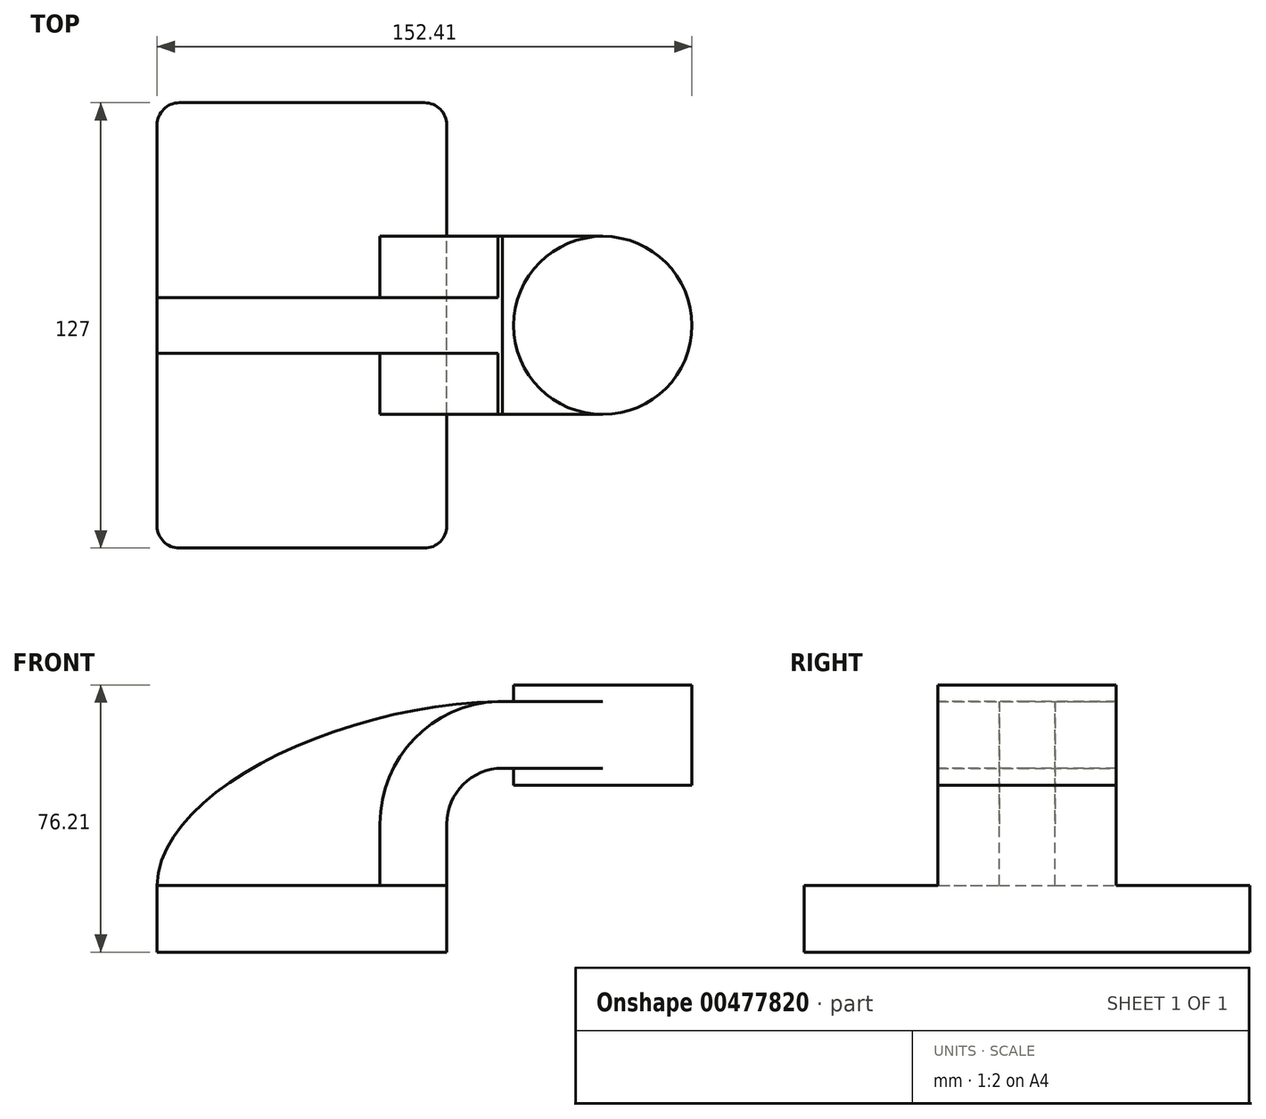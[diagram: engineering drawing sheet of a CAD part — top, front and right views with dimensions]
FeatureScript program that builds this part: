
annotation { "Feature Type Name" : "Feature", "Feature Type Description" : "" }
export const myFeature = defineFeature(function(context is Context, id is Id, definition is map)
    precondition{}
    {
        {
            var Q0;
            Q0=qCreatedBy(makeId("Front.planeOp"),FACE);
            var sketch = newSketch(context, id + "F0", { "sketchPlane" : qUnion([Q0])});
            skLineSegment(sketch, "E0.bottom", {"start": v(60.32, 66.67) * mm, "end": v(111.12, 66.67) * mm});
            skLineSegment(sketch, "E0.top", {"start": v(60.32, 38.1) * mm, "end": v(111.12, 38.1) * mm});
            skLineSegment(sketch, "E0.right", {"start": v(111.12, 66.68) * mm, "end": v(111.12, 38.1) * mm});
            skPoint(sketch, "E0.middle", {"position": v(85.72, 52.39) * mm});
            skLineSegment(sketch, "E1.bottom", {"start": v(-41.28, 9.52) * mm, "end": v(41.27, 9.53) * mm});
            skLineSegment(sketch, "E1.top", {"start": v(-41.28, -9.53) * mm, "end": v(41.28, -9.53) * mm});
            skLineSegment(sketch, "E1.left", {"start": v(-41.28, 9.52) * mm, "end": v(-41.28, -9.53) * mm});
            skLineSegment(sketch, "E1.right", {"start": v(41.28, 9.53) * mm, "end": v(41.28, -9.52) * mm});
            skPoint(sketch, "E1.middle", {"position": v(0, 0) * mm});
            skLineSegment(sketch, "E2", {"start": v(41.27, 9.53) * mm, "end": v(41.27, 27.06) * mm});
            skArc(sketch, "E3", {"start": v(41.28, 27.06) * mm, "mid": v(45.92, 38.29) * mm, "end": v(57.15, 42.93) * mm});
            skLineSegment(sketch, "E4", {"start": v(57.15, 42.93) * mm, "end": v(85.73, 42.93) * mm});
            skFitSpline(sketch, "E5", {"points": [v(-41.28, 9.53) * mm, v(57.15, 61.98) * mm], "startDerivative": vector(2.18, 82.42) * mm, "endDerivative": vector(136.08, 1.9) * mm});
            skLineSegment(sketch, "E6.0", {"start": v(-47.63, 9.52) * mm, "end": v(-47.63, -9.53) * mm});
            skLineSegment(sketch, "E7.0", {"start": v(57.15, 61.98) * mm, "end": v(85.73, 61.98) * mm});
            skArc(sketch, "E7.1", {"start": v(22.23, 27.06) * mm, "mid": v(32.45, 51.76) * mm, "end": v(57.15, 61.98) * mm});
            skLineSegment(sketch, "E7.2", {"start": v(22.23, 9.53) * mm, "end": v(22.23, 27.06) * mm});
            skLineSegment(sketch, "E8", {"start": v(85.72, 38.1) * mm, "end": v(85.72, 66.67) * mm});
            skLineSegment(sketch, "E9", {"start": v(60.32, 66.67) * mm, "end": v(60.32, 61.98) * mm});
            skLineSegment(sketch, "E10", {"start": v(60.32, 42.93) * mm, "end": v(60.32, 38.1) * mm});
            skSolve(sketch);
        }
        {
            var Q0;
            Q0=makeQuery(id+"F0.imprint","IMPRINT",FACE,{"disambiguationData":[TD([[makeQuery(id+"F0.imprint","IMPRINT",EDGE,{"derivedFrom":sQuery(id+"F0.wireOp",EDGE,"E1.bottom")}),-1.0]])]});
            extrude(context, id + "F1", {"entities" : qUnion([Q0]), "endBound" : BoundingType.SYMMETRIC, "depth" : 127 * mm});
        }
        {
            var Q0;
            {var subQ0=sQuery(id+"F0.wireOp",EDGE,"E2");Q0=makeQuery(id+"F0.imprint","IMPRINT",FACE,{"disambiguationData":[TD([[makeQuery(id+"F0.imprint","IMPRINT",EDGE,{"derivedFrom":subQ0}),1.0]])]});}
            var Q1;
            {var subQ5=sQuery(id+"F0.wireOp",EDGE,"Z56nLSGl-zMS4-q6ac-4DDA-MC8ZnwYVUiy6");Q1=makeQuery(id+"F0.imprint","IMPRINT",FACE,{"disambiguationData":[TD([[makeQuery(id+"F0.imprint","IMPRINT",EDGE,{"derivedFrom":subQ5}),-1.0]])]});}
            extrude(context, id + "F2", {"entities" : qUnion([Q0, Q1]), "operationType" : NewBodyOperationType.ADD, "endBound" : BoundingType.SYMMETRIC, "depth" : 50.8 * mm});
        }
        {
            var Q0;
            {var subQ3=sQuery(id+"F0.wireOp",EDGE,"E7.2");Q0=makeQuery(id+"F0.imprint","IMPRINT",FACE,{"disambiguationData":[TD([[makeQuery(id+"F0.imprint","IMPRINT",EDGE,{"derivedFrom":subQ3}),1.0]])]});}
            extrude(context, id + "F3", {"entities" : qUnion([Q0]), "operationType" : NewBodyOperationType.ADD, "endBound" : BoundingType.SYMMETRIC, "depth" : 15.88 * mm});
        }
        {
            var Q0;
            {var subQ0=sQuery(id+"F0.wireOp",EDGE,"E0.right");Q0=makeQuery(id+"F0.imprint","IMPRINT",FACE,{"disambiguationData":[TD([[makeQuery(id+"F0.imprint","IMPRINT",EDGE,{"derivedFrom":subQ0}),-1.0]])]});}
            var Q1;
            Q1=sQuery(id+"F0.wireOp",EDGE,"E8");
            revolve(context, id + "F4", {"operationType" : NewBodyOperationType.ADD, "entities" : qUnion([Q0]), "axis" : qUnion([Q1]), "revolveType" : RevolveType.FULL});
        }
        {
            var Q0;
            Q0=makeQuery(id+"F1.opExtrude","CAP_EDGE",EDGE,{"disambiguationData":[OSD([sQuery(id+"F0.wireOp",EDGE,"E1.right")])],"isStart":false});
            var Q1;
            Q1=makeQuery(id+"F1.opExtrude","CAP_EDGE",EDGE,{"disambiguationData":[OSD([sQuery(id+"F0.wireOp",EDGE,"E1.left")])],"isStart":false});
            var Q2;
            Q2=makeQuery(id+"F1.opExtrude","CAP_EDGE",EDGE,{"disambiguationData":[OSD([sQuery(id+"F0.wireOp",EDGE,"E1.left")])],"isStart":true});
            var Q3;
            Q3=makeQuery(id+"F1.opExtrude","CAP_EDGE",EDGE,{"disambiguationData":[OSD([sQuery(id+"F0.wireOp",EDGE,"E1.right")])],"isStart":true});
            fillet(context, id + "F5", {"entities" : qUnion([Q0, Q1, Q2, Q3]), "radius" : 6.35 * mm, "tangentPropagation" : true, "allowEdgeOverflow" : false});
        }
    });
